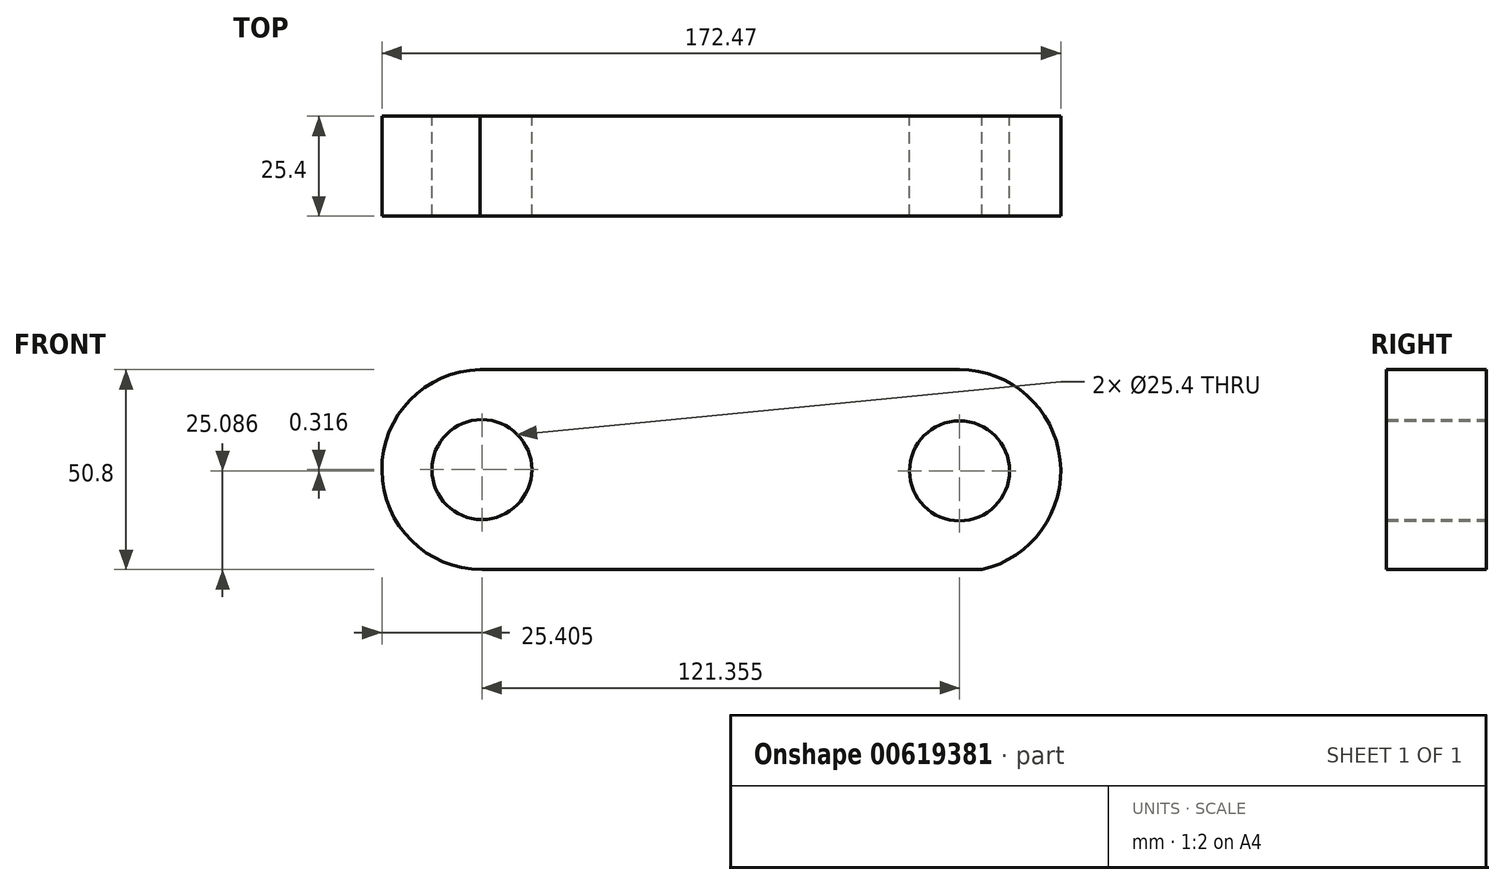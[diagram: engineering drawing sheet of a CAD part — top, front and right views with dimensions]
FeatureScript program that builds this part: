
annotation { "Feature Type Name" : "Feature", "Feature Type Description" : "" }
export const myFeature = defineFeature(function(context is Context, id is Id, definition is map)
    precondition{}
    {
        {
            var Q0;
            Q0=qCreatedBy(makeId("Front.planeOp"),FACE);
            var sketch = newSketch(context, id + "F0", { "sketchPlane" : qUnion([Q0])});
            skLineSegment(sketch, "E0", {"start": v(-35.43, 50.8) * mm, "end": v(86.36, 50.8) * mm});
            skLineSegment(sketch, "E1", {"start": v(-35, 0) * mm, "end": v(92, 0) * mm});
            skArc(sketch, "E2", {"start": v(-35.43, 50.8) * mm, "mid": v(-60.4, 25.18) * mm, "end": v(-35, 0) * mm});
            skArc(sketch, "E3", {"start": v(92, 0) * mm, "mid": v(111.92, 27.93) * mm, "end": v(86.36, 50.8) * mm});
            skCircle(sketch, "E4", {"center": v(-35, 25.4) * mm, "radius": 12.7 * mm});
            skCircle(sketch, "E5", {"center": v(86.36, 25.09) * mm, "radius": 12.7 * mm});
            skSolve(sketch);
        }
        {
            var Q0;
            Q0=makeQuery(id+"F0.imprint","IMPRINT",FACE,{"disambiguationData":[TD([[makeQuery(id+"F0.imprint","IMPRINT",EDGE,{"derivedFrom":sQuery(id+"F0.wireOp",EDGE,"E0")}),-1.0]])]});
            extrude(context, id + "F1", {"entities" : qUnion([Q0]), "depth" : 25.4 * mm, "offsetDistance" : 25.4 * mm});
        }
    });
